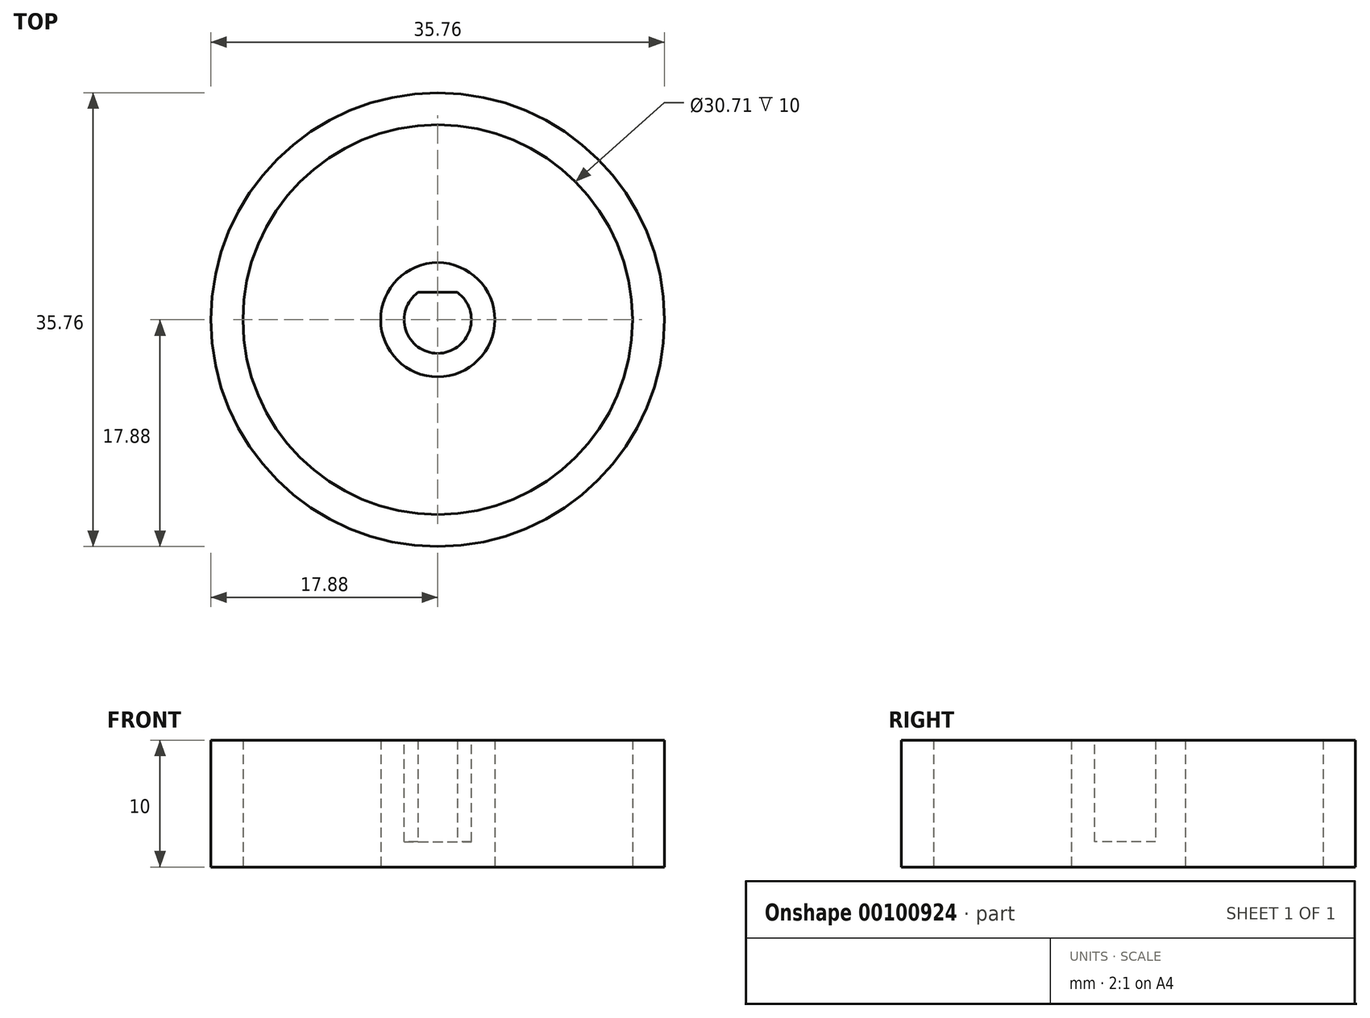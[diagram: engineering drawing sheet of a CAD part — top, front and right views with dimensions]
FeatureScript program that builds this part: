
annotation { "Feature Type Name" : "Feature", "Feature Type Description" : "" }
export const myFeature = defineFeature(function(context is Context, id is Id, definition is map)
    precondition{}
    {
        {
            var Q0;
            Q0=qCreatedBy(makeId("Top.planeOp"),FACE);
            var sketch = newSketch(context, id + "F0", { "sketchPlane" : qUnion([Q0])});
            skCircle(sketch, "E0", {"center": v(0, 0) * mm, "radius": 4.5 * mm});
            skSolve(sketch);
        }
        {
            var Q0;
            Q0=makeQuery(id+"F0.imprint","IMPRINT",FACE,{"disambiguationData":[TD([[makeQuery(id+"F0.imprint","IMPRINT",EDGE,{"derivedFrom":sQuery(id+"F0.wireOp",EDGE,"E0")}),1.0]])]});
            extrude(context, id + "F1", {"entities" : qUnion([Q0]), "depth" : 10 * mm});
        }
        {
            var Q0;
            Q0=makeQuery(id+"F1.opExtrude","CAP_FACE",FACE,{"disambiguationData":[OSD([sQuery(id+"F0.wireOp",EDGE,"E0")])],"isStart":false});
            var sketch = newSketch(context, id + "F2", { "sketchPlane" : qUnion([Q0])});
            skCircle(sketch, "E1", {"center": v(0, 0) * mm, "radius": 2.65 * mm});
            skSolve(sketch);
        }
        {
            var Q0;
            Q0=makeQuery(id+"F2.imprint","IMPRINT",FACE,{"disambiguationData":[TD([[makeQuery(id+"F2.imprint","IMPRINT",EDGE,{"derivedFrom":sQuery(id+"F2.wireOp",EDGE,"E1")}),1.0]])]});
            extrude(context, id + "F3", {"entities" : qUnion([Q0]), "operationType" : NewBodyOperationType.REMOVE, "oppositeDirection" : true, "depth" : 8 * mm});
        }
        {
            var Q0;
            Q0=makeQuery(id+"F3.boolean.opBoolean","COPY",FACE,{"derivedFrom":makeQuery(id+"F3.opExtrude","CAP_FACE",FACE,{"disambiguationData":[OSD([sQuery(id+"F2.wireOp",EDGE,"E1")])],"isStart":false})});
            var sketch = newSketch(context, id + "F4", { "sketchPlane" : qUnion([Q0])});
            skLineSegment(sketch, "E2", {"start": v(-1.55, 2.15) * mm, "end": v(1.55, 2.15) * mm});
            skArc(sketch, "E3", {"start": v(-1.55, 2.15) * mm, "mid": v(0, 2.65) * mm, "end": v(1.55, 2.15) * mm});
            skSolve(sketch);
        }
        {
            var Q0;
            Q0=makeQuery(id+"F4.imprint","IMPRINT",FACE,{"disambiguationData":[TD([[makeQuery(id+"F4.imprint","IMPRINT",EDGE,{"derivedFrom":sQuery(id+"F4.wireOp",EDGE,"E2")}),1.0]])]});
            var Q1;
            Q1=makeQuery(id+"F1.opExtrude","CAP_FACE",FACE,{"disambiguationData":[OSD([sQuery(id+"F0.wireOp",EDGE,"E0")])],"isStart":false});
            extrude(context, id + "F5", {"entities" : qUnion([Q0]), "operationType" : NewBodyOperationType.ADD, "endBound" : BoundingType.UP_TO_SURFACE, "endBoundEntityFace" : qUnion([Q1]), "depth" : 25.4 * mm});
        }
        {
            var Q0;
            Q0=qCreatedBy(makeId("Top.planeOp"),FACE);
            var sketch = newSketch(context, id + "F6", { "sketchPlane" : qUnion([Q0])});
            skCircle(sketch, "E4", {"center": v(0, 0) * mm, "radius": 15.36 * mm});
            skCircle(sketch, "E5", {"center": v(0, 0) * mm, "radius": 17.88 * mm});
            skSolve(sketch);
        }
        {
            var Q0;
            Q0=makeQuery(id+"F6.imprint","IMPRINT",FACE,{"disambiguationData":[TD([[makeQuery(id+"F6.imprint","IMPRINT",EDGE,{"derivedFrom":sQuery(id+"F6.wireOp",EDGE,"E4")}),-1.0]])]});
            var Q1;
            Q1=makeQuery(id+"F5.boolean.opBoolean","MERGE",FACE,{"derivedFrom":[makeQuery(id+"F1.opExtrude","CAP_FACE",FACE,{"disambiguationData":[OSD([sQuery(id+"F0.wireOp",EDGE,"E0")])],"isStart":false}),makeQuery(id+"F5.opExtrude","CAP_FACE",FACE,{"disambiguationData":[OSD([sQuery(id+"F4.wireOp",EDGE,"E2"),sQuery(id+"F4.wireOp",EDGE,"E3")])],"isStart":false})]});
            extrude(context, id + "F7", {"entities" : qUnion([Q0]), "operationType" : NewBodyOperationType.ADD, "endBound" : BoundingType.UP_TO_SURFACE, "endBoundEntityFace" : qUnion([Q1]), "depth" : 25.4 * mm});
        }
    });
